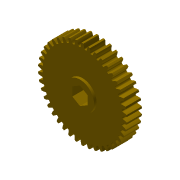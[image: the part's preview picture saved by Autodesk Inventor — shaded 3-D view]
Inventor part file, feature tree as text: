
AUTODESK INVENTOR PART (.ipt)
format: ipt  version: 2013 (Build 170138000, 138)  size: 487,936 bytes
history: native  units: in
note: dims shown in document units (in); Inventor stores cm internally (conversion verified against a paired STEP export)
features: other x2, extrude x1, imported_body x1, sketch x1
ambient origin geometry x8: Origin, YZ Plane, XZ Plane, XY Plane, X Axis, Y Axis, Z Axis, Center Point
feature tree (5):
  other  "Cut-Extrude4"
  other  "217-3216-STEP1"
  extrude  "Extrusion1"  Depth=1.0in TaperAngle=0.0deg
  imported_body  "Base1"
  sketch  "Sketch1"  dims[d0=0.378in d2=1.0in d3=0.0in]
